# Revit family: Hager-Univers-IP54-D205-H1700-Cl.I-Encl-NoHosted-CH-it
name_source: partatom
category: Electrical Equipment
units: mm (PartAtom-declared; Revit-internal decimal feet)

## family parameters
Always vertical = Yes
Cut with Voids When Loaded = No
Panel Configuration = Two Columns, Circuits Across
Part Type = Panelboard
Room Calculation Point = No
Round Connector Dimension = Use Diameter
Shared = No
Work Plane-Based = Yes

## types (5) — shared parameters
Default Elevation = 1219 mm
EF000003 - Tipo di montaggio = EV000384 - A parete
EF000007 - colore = EV000202 - bianco
EF000040 - Altezza = 1700 mm  [stored 5.57743 ft]
EF000049 - profondità = 205 mm  [stored 0.672572 ft]
EF000116 - numero RAL = 9010
EF000118 - con piastra di montaggio = No
EF000218 - profondità di incasso = 205 mm  [stored 0.672572 ft]
EF000266 - numero di file = 11
EF000339 - tipo di copertura = EV001012 - coperchio
EF001088 - possibilità di applicazione = Yes
EF001131 - profondità interna = 205 mm  [stored 0.672572 ft]
EF001596 - Attacco Lampada = EV000179 - acciaio
EF001613 - Integrità del circuito = EV000494 - senza
EF003532 - adatto per uso esterno = No
EF004293 - resistenza agli urti = EV006815 - IK09
EF005474 - grado di protezione (IP) = EV006419 - IP54
EF006244 - coperchio/porta trasparente = No
EF006306 - con serratura = No
EF007800 - adatto per parafulmine = No
EF009170 - spessore materiale scatola = 1 mm  [stored 0.00328084 ft]
EF009171 - spessore materiale porta/coperchio = 1 mm  [stored 0.00328084 ft]
EF009212 - esecuzione coperchio = EV000116 - chiuso
EF015940 - Coprire con rilascio di sovrapressione = No
HG000002 - Con porta = Yes
HG000003 - Gamma = Univers
HG000006 - Ad incasso = No
HG000010 - Porte asimmetriche = No
HG000023 - Custodia a doppia sezione = No
HG000024 - Altezza della sezione inferiore = 600 mm
HG000026 - A pavimento = No
Manufacturer = Hager
Type Comments = Univers
zero-valued in all types: HG000027 - Altezza dello zoccolo

## per-type parameters (varying)
| type | EF000008 - Larghezza | EF000437 - numero di ingressi per conduttori | EF002950 - Numero moduli DIN | EF004427 - numero di moduli | EF004464 - tipo di porta | EF008873 - corrente nominale (In) | EF009554 - numero delle aperture per la piastra della flangia | HG000004 - Codice produttore | HG000009 - Porta doppia a battente |
| A parete IP54 L1050 A1700 P205  - FP14TW2 | 1050 mm | 8 | 48 | 528 | EV003602 - doppio | 400 A | 8 | FP14TW2 | Yes |
| A parete IP54 L1300 A1700 P205  - FP15TW2 | 1300 mm  [stored 4.26509 ft] | 10 | 60 | 660 | EV003602 - doppio | 400 A | 10 | FP15TW2 | No |
| A parete IP54 L300 A1700 P205  - FP11TW2 | 300 mm | 2 | 12 | 132 | EV002646 - singolo | 250 A | 2 | FP11TW2 | No |
| A parete IP54 L550 A1700 P205  - FP12TW2 | 550 mm | 4 | 24 | 264 | EV002646 - singolo | 250 A | 4 | FP12TW2 | No |
| A parete IP54 L800 A1700 P205  - FP13TW2 | 800 mm  [stored 2.62467 ft] | 6 | 36 | 396 | EV002646 - singolo | 400 A | 6 | FP13TW2 | No |

note: [stored X ft] marks values corroborated as IEEE doubles in the binary element streams (Revit-internal decimal feet)

## geometry (parser evidence)
native form markers: Blend x4, Sweep x11
no freeform markers — native parametric forms only
